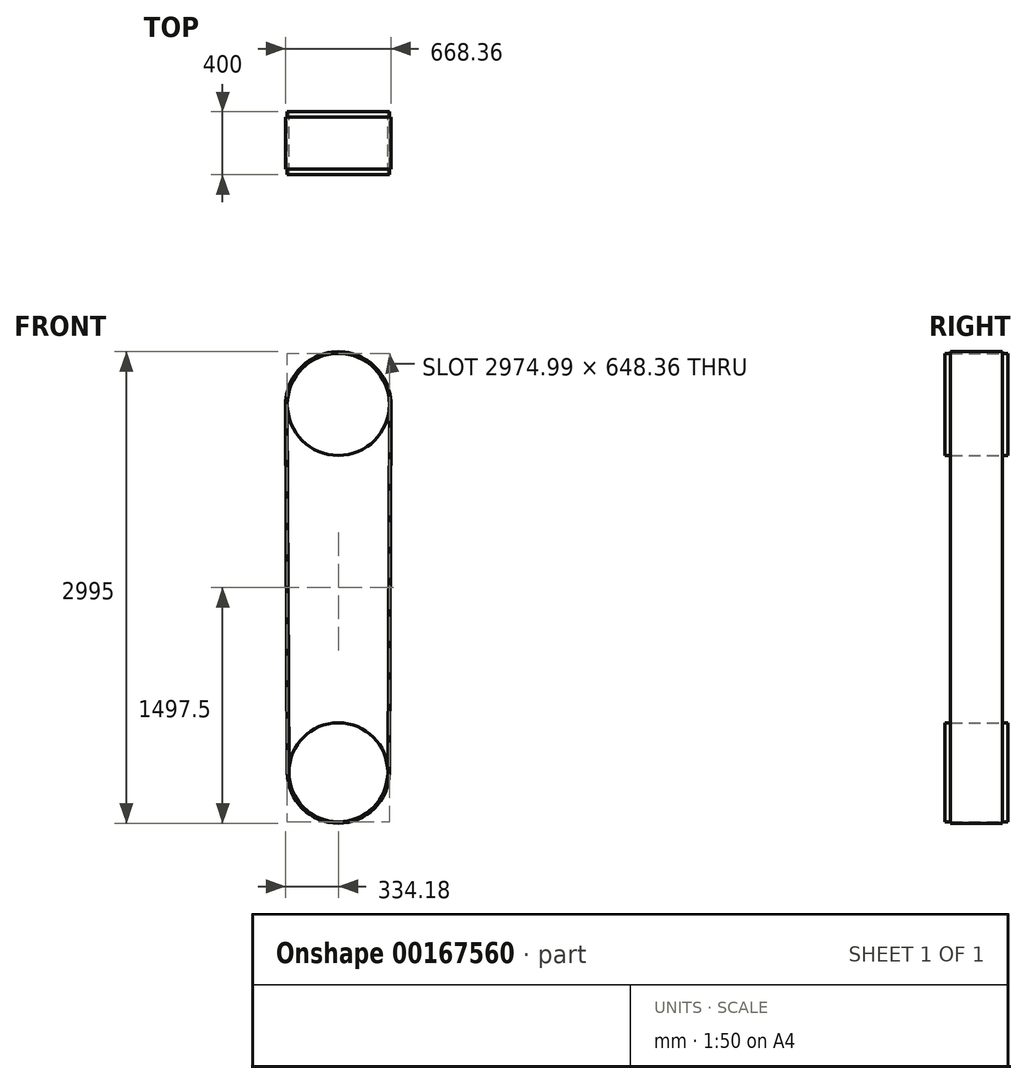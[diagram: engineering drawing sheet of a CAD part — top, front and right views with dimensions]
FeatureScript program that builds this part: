
annotation { "Feature Type Name" : "Feature", "Feature Type Description" : "" }
export const myFeature = defineFeature(function(context is Context, id is Id, definition is map)
    precondition{}
    {
        {
            var Q0;
            Q0=qCreatedBy(makeId("Front.planeOp"),FACE);
            var sketch = newSketch(context, id + "F0", { "sketchPlane" : qUnion([Q0])});
            skCircle(sketch, "E0", {"center": v(0, 1276.9) * mm, "radius": 324.18 * mm});
            skArc(sketch, "E1", {"start": v(-324.18, -1061.12) * mm, "mid": v(0, -1383.92) * mm, "end": v(324.18, -1061.12) * mm});
            skCircle(sketch, "E2.0", {"center": v(0, -1059.73) * mm, "radius": 314.18 * mm});
            skLineSegment(sketch, "E3", {"start": v(-334.18, 1275.46) * mm, "end": v(-324.18, -1061.12) * mm});
            skLineSegment(sketch, "E4", {"start": v(0, 1276.9) * mm, "end": v(0, -1059.73) * mm, "construction": true});
            skLineSegment(sketch, "E5.MirrorCS", {"start": v(334.18, 1275.46) * mm, "end": v(324.18, -1061.12) * mm});
            skLineSegment(sketch, "E6.0", {"start": v(324.18, 1275.5) * mm, "end": v(314.18, -1061.08) * mm});
            skLineSegment(sketch, "E7.0", {"start": v(-324.18, 1275.5) * mm, "end": v(-314.18, -1061.08) * mm});
            skArc(sketch, "E8.trimOffspring", {"start": v(334.18, 1275.46) * mm, "mid": v(0, 1611.08) * mm, "end": v(-334.18, 1275.46) * mm});
            skSolve(sketch);
        }
        {
            var Q0;
            {var subQ0=sQuery(id+"F0.wireOp",EDGE,"E2.0");var subQ1=makeQuery(id+"F0.imprint","INTERSECT",VERTEX,{"derivedFrom":[subQ0,sQuery(id+"F0.wireOp",EDGE,"E6.0")]});Q0=makeQuery(id+"F0.imprint","IMPRINT",FACE,{"disambiguationData":[TD([[makeQuery(id+"F0.imprint","IMPRINT",EDGE,{"disambiguationData":[TD([[subQ1,1.0]])],"derivedFrom":subQ0}),1.0]])]});}
            var Q1;
            {var subQ0=sQuery(id+"F0.wireOp",EDGE,"E0");var subQ1=makeQuery(id+"F0.imprint","INTERSECT",VERTEX,{"derivedFrom":[subQ0,sQuery(id+"F0.wireOp",EDGE,"E6.0")]});Q1=makeQuery(id+"F0.imprint","IMPRINT",FACE,{"disambiguationData":[TD([[makeQuery(id+"F0.imprint","IMPRINT",EDGE,{"disambiguationData":[TD([[subQ1,1.0]])],"derivedFrom":subQ0}),1.0]])]});}
            extrude(context, id + "F1", {"entities" : qUnion([Q0, Q1]), "endBound" : BoundingType.SYMMETRIC, "depth" : 400 * mm});
        }
        {
            var Q0;
            Q0 = qSketchRegion(id + "F0", true);
            extrude(context, id + "F2", {"entities" : qUnion([Q0]), "endBound" : BoundingType.SYMMETRIC, "depth" : 330 * mm});
        }
    });
